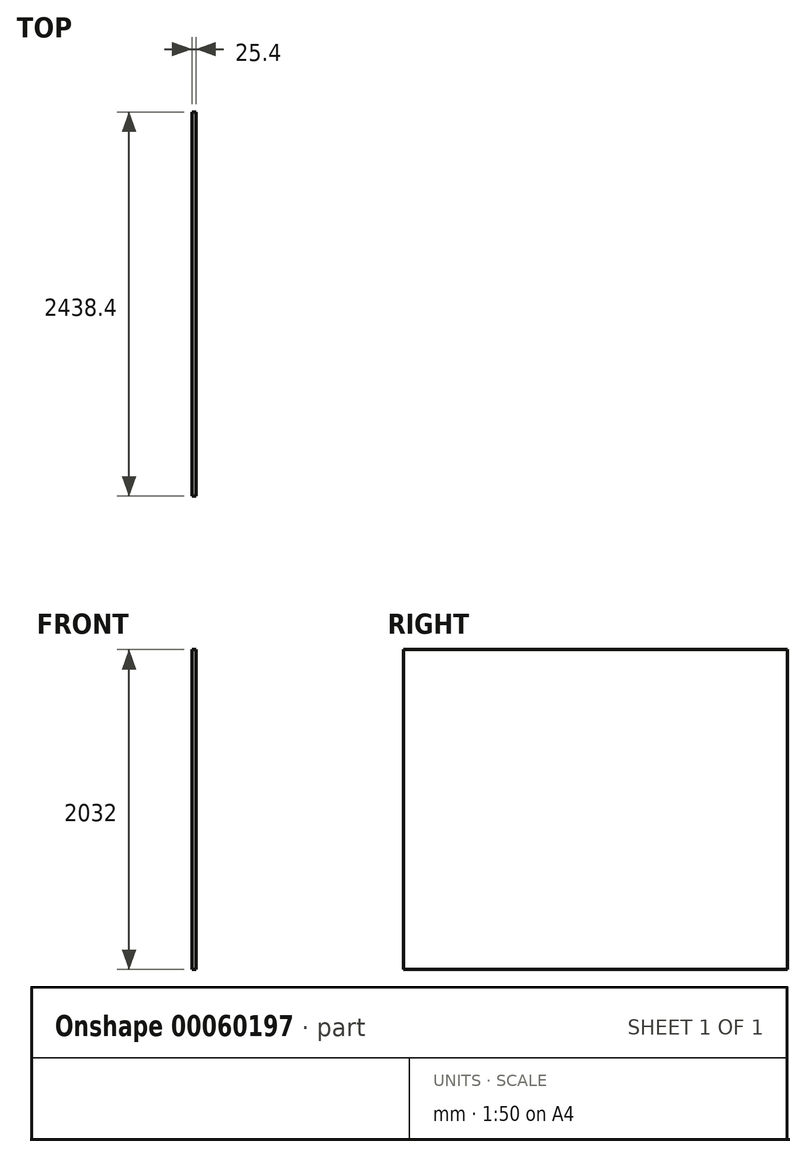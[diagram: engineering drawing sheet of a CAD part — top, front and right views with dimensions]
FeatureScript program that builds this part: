
annotation { "Feature Type Name" : "Feature", "Feature Type Description" : "" }
export const myFeature = defineFeature(function(context is Context, id is Id, definition is map)
    precondition{}
    {
        {
            var Q0;
            Q0=qCreatedBy(makeId("Right.planeOp"),FACE);
            var sketch = newSketch(context, id + "F0", { "sketchPlane" : qUnion([Q0])});
            skLineSegment(sketch, "E0.rect.bottom", {"start": v(1219.2, 1016) * mm, "end": v(-1219.2, 1016) * mm});
            skLineSegment(sketch, "E0.rect.top", {"start": v(1219.2, -1016) * mm, "end": v(-1219.2, -1016) * mm});
            skLineSegment(sketch, "E0.rect.left", {"start": v(1219.2, 1016) * mm, "end": v(1219.2, -1016) * mm});
            skLineSegment(sketch, "E0.rect.right", {"start": v(-1219.2, 1016) * mm, "end": v(-1219.2, -1016) * mm});
            skPoint(sketch, "E0.rect.middle", {"position": v(0, 0) * mm});
            skSolve(sketch);
        }
        {
            var Q0;
            Q0=makeQuery(id+"F0.imprint","IMPRINT",FACE,{"disambiguationData":[TD([[makeQuery(id+"F0.imprint","IMPRINT",EDGE,{"derivedFrom":sQuery(id+"F0.wireOp",EDGE,"E0.rect.bottom")}),1.0]])]});
            extrude(context, id + "F1", {"entities" : qUnion([Q0]), "depth" : 25.4 * mm});
        }
    });
